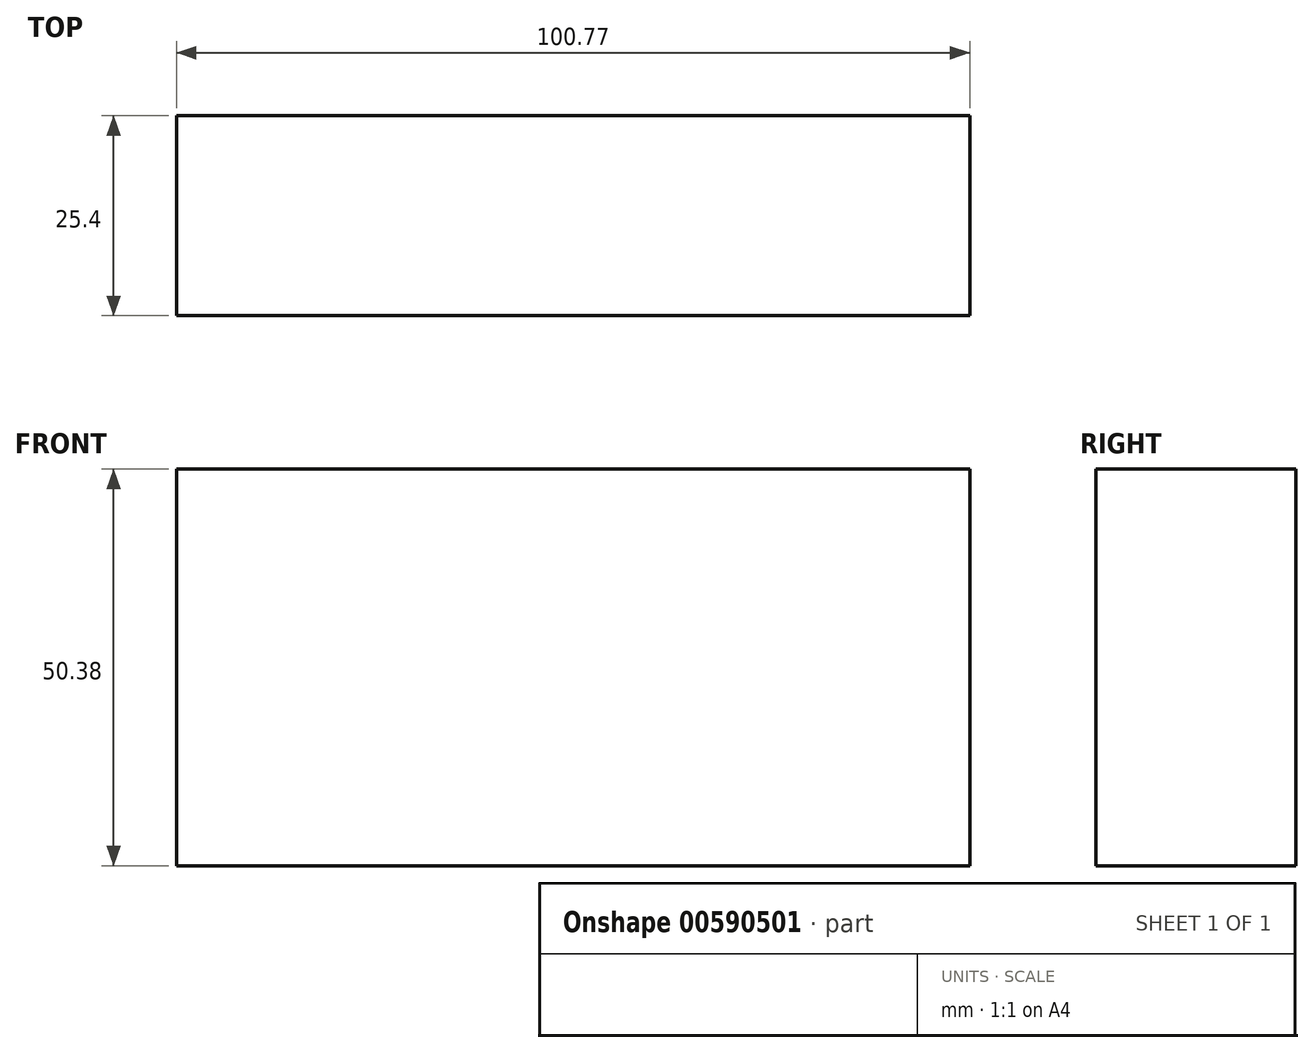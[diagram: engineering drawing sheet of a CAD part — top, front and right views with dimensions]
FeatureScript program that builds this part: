
annotation { "Feature Type Name" : "Feature", "Feature Type Description" : "" }
export const myFeature = defineFeature(function(context is Context, id is Id, definition is map)
    precondition{}
    {
        {
            var Q0;
            Q0=qCreatedBy(makeId("Front.planeOp"),FACE);
            var sketch = newSketch(context, id + "F0", { "sketchPlane" : qUnion([Q0])});
            skLineSegment(sketch, "E0.bottom", {"start": v(-43.82, 33.74) * mm, "end": v(56.95, 33.74) * mm});
            skLineSegment(sketch, "E0.top", {"start": v(-43.82, -16.64) * mm, "end": v(56.95, -16.64) * mm});
            skLineSegment(sketch, "E0.left", {"start": v(-43.82, 33.74) * mm, "end": v(-43.82, -16.64) * mm});
            skLineSegment(sketch, "E0.right", {"start": v(56.95, 33.74) * mm, "end": v(56.95, -16.64) * mm});
            skSolve(sketch);
        }
        {
            var Q0;
            Q0 = qSketchRegion(id + "F0", true);
            extrude(context, id + "F1", {"entities" : qUnion([Q0]), "depth" : 25.4 * mm, "offsetDistance" : 25.4 * mm});
        }
    });
